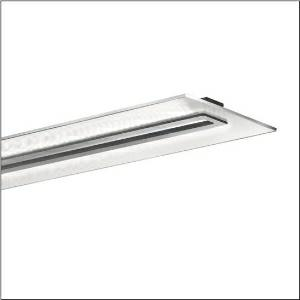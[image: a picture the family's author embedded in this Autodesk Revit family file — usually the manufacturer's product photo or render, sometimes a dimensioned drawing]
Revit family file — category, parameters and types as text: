
# Revit family: vega_r__11_5mn238dlc003_c003
name_source: partatom
category: Lighting Fixtures
units: mm (PartAtom-declared; Revit-internal decimal feet)

## family parameters
Cut with Voids When Loaded = No
Host = Face
Light Source = No
Part Type = Normal
Room Calculation Point = No
Round Connector Dimension = Use Diameter
Shared = No

## types (1)
- --- (1 x LED 3000K / CRI = 80 (unbekannt), 4300 lm, 3000K)
    Apparent Load = 35 VA
    CIE Flux Codes = 61 86 97 62 100
    Color Rendering = 80
    Color Temperature = 3000K
    Default Elevation = 1800 mm
    Description = Vega® 11, office luminaire, primary light control with prismatic reflector, of PMMA, transparent prismatic structure, CAT 2 (L<= 1500cd/m²), light emission: direct/indirect distribution, primary light characteristic: symmetric, installation type: suspended mounting, surface-mounted, LED, rated luminous flux: 4.300lm, luminous efficacy: 123lm/W, light colour: 830, colour temperature: 3000K, control gear: DALI, with terminal, 3+2-pole, max. 2.5mm², mains connection: 230V, AC, 50Hz, connection cable inclusive, cable length: 1,5m, rated input power: 35W, luminaire housing, rectangular, rounded, of aluminium section, anodised, metallic grey (RAL 9006), length: 1.250mm, width: 350mm, height: 43mm, luminaire housing, lower part, of aluminium section, anodised, metallic grey (RAL 9006), of PC, grey, protection rating (complete): IP20, insulation class (complete): insulation class I (protective earthing), certification: CE, standard: EN 50419, packaging unit: 1 piece
    Height = 40 mm  [stored 0.131234 ft]
    Lamp = 1 x LED 3000K / CRI >= 80 (unbekannt)
    Lamp Light Flux = 4300 lm
    Lamp count = 1
    Length = 1250 mm
    Luminous efficacy = 123 lm/W
    Manufacturer = Siteco
    ModVariant = No
    Model = 5MN238DLC003
    Mounting Place = Ceiling
    Mounting Type = Pendant
    Number of Poles = 1
    OnlyDefault = Yes
    Power Factor = 1
    Product Name = Vega® 11
    Product group = office luminaire | ceiling pendant
    ProductGroupID = 904
    Protection Class = Protection class I
    Protection Degree = IP 20
    RLX_Detail_Level = 1
    RLX_Emergency_Light_Flux = 0 lm
    RLX_Emergency_Type = 0
    RLX_Emergency_Type_DB = No
    RlxData = <blob elided: 62753 chars, md5=ef3cebb8>
    Socket = socket
    Standby Power = 0 W
    System Light Flux = 4300 lm
    System Power = 35 W
    Type Comments = factory setting: luminous flux: 100 % | dim-lin: 254 | 260 mA
    Type Image = l_1004807.jpg
    URL = http://relux.com
    VarID = @adj_203932
    Voltage = 0 V
    Weight = 0.00 kg
    Width = 350 mm

note: [stored X ft] marks values corroborated as IEEE doubles in the binary element streams (Revit-internal decimal feet)

## geometry (parser evidence)
native form markers: Blend x4, Sweep x13
no freeform markers — native parametric forms only
